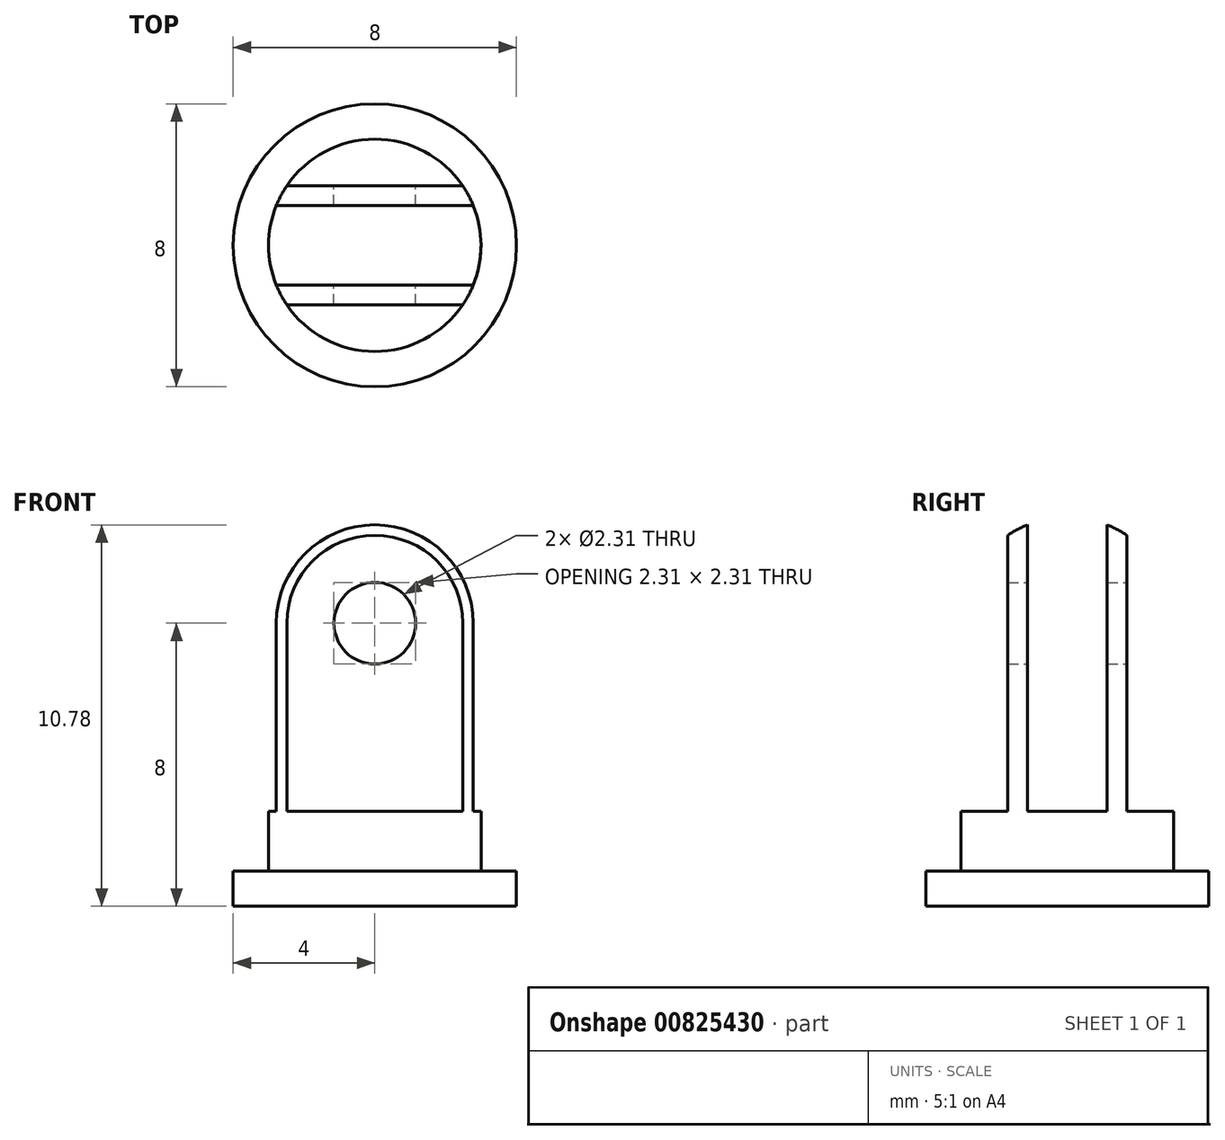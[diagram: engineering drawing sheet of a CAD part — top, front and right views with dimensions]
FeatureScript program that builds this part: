
annotation { "Feature Type Name" : "Feature", "Feature Type Description" : "" }
export const myFeature = defineFeature(function(context is Context, id is Id, definition is map)
    precondition{}
    {
        {
            var Q0;
            Q0=qCreatedBy(makeId("Top.planeOp"),FACE);
            var sketch = newSketch(context, id + "F0", { "sketchPlane" : qUnion([Q0])});
            skCircle(sketch, "E0", {"center": v(0, 0) * mm, "radius": 4 * mm});
            skSolve(sketch);
        }
        {
            var Q0;
            Q0=makeQuery(id+"F0.imprint","IMPRINT",FACE,{"disambiguationData":[TD([[makeQuery(id+"F0.imprint","IMPRINT",EDGE,{"derivedFrom":sQuery(id+"F0.wireOp",EDGE,"E0")}),1.0]])]});
            extrude(context, id + "F1", {"entities" : qUnion([Q0]), "depth" : 1 * mm, "offsetDistance" : 25 * mm});
        }
        {
            var Q0;
            Q0=makeQuery(id+"F1.opExtrude","CAP_FACE",FACE,{"disambiguationData":[OSD([sQuery(id+"F0.wireOp",EDGE,"E0")])],"isStart":false});
            var sketch = newSketch(context, id + "F2", { "sketchPlane" : qUnion([Q0])});
            skCircle(sketch, "E1", {"center": v(0, 0) * mm, "radius": 3 * mm});
            skSolve(sketch);
        }
        {
            var Q0;
            Q0=makeQuery(id+"F2.imprint","IMPRINT",FACE,{"disambiguationData":[TD([[makeQuery(id+"F2.imprint","IMPRINT",EDGE,{"derivedFrom":sQuery(id+"F2.wireOp",EDGE,"E1")}),1.0]])]});
            extrude(context, id + "F3", {"entities" : qUnion([Q0]), "operationType" : NewBodyOperationType.ADD, "depth" : 10 * mm, "offsetDistance" : 25 * mm});
        }
        {
            var Q0;
            Q0=makeQuery(id+"F3.opExtrude","CAP_EDGE",EDGE,{"disambiguationData":[OSD([sQuery(id+"F2.wireOp",EDGE,"E1")])],"isStart":false});
            fillet(context, id + "F4", {"entities" : qUnion([Q0]), "radius" : 3 * mm, "tangentPropagation" : true, "allowEdgeOverflow" : false});
        }
        {
            var Q0;
            Q0=qCreatedBy(makeId("Right.planeOp"),FACE);
            var sketch = newSketch(context, id + "F5", { "sketchPlane" : qUnion([Q0])});
            skLineSegment(sketch, "E2", {"start": v(0, 29.4) * mm, "end": v(0, 0) * mm, "construction": true});
            skLineSegment(sketch, "E3.bottom", {"start": v(1.12, 2.68) * mm, "end": v(-1.12, 2.68) * mm});
            skLineSegment(sketch, "E3.top", {"start": v(1.12, 13.42) * mm, "end": v(-1.12, 13.42) * mm});
            skLineSegment(sketch, "E3.left", {"start": v(1.12, 2.68) * mm, "end": v(1.12, 13.42) * mm});
            skLineSegment(sketch, "E3.right", {"start": v(-1.12, 2.68) * mm, "end": v(-1.12, 13.42) * mm});
            skPoint(sketch, "E3.middle", {"position": v(0, 8.05) * mm});
            skLineSegment(sketch, "E4.bottom", {"start": v(-1.68, 13.42) * mm, "end": v(-3.14, 13.42) * mm});
            skLineSegment(sketch, "E4.top", {"start": v(-1.68, 2.68) * mm, "end": v(-3.14, 2.68) * mm});
            skLineSegment(sketch, "E4.left", {"start": v(-1.68, 13.42) * mm, "end": v(-1.68, 2.68) * mm});
            skLineSegment(sketch, "E4.right", {"start": v(-3.14, 13.42) * mm, "end": v(-3.14, 2.68) * mm});
            skPoint(sketch, "E4.middle", {"position": v(-2.4, 8.05) * mm});
            skPoint(sketch, "E5.middle", {"position": v(2.31, 8.05) * mm});
            skPoint(sketch, "E5.middle.positionSnap0", {"position": v(1.12, 8.05) * mm});
            skPoint(sketch, "E5.centerSnap0", {"position": v(1.12, 8.05) * mm});
            skPoint(sketch, "E5.right.start.orphan", {"position": v(3.1, 13.42) * mm});
            skPoint(sketch, "E5.top.end.orphan", {"position": v(3.1, 2.68) * mm});
            skPoint(sketch, "E5.left.end.orphan", {"position": v(1.53, 2.68) * mm});
            skPoint(sketch, "E5.left.start.orphan", {"position": v(1.53, 13.42) * mm});
            skLineSegment(sketch, "E6.MirrorCS", {"start": v(1.68, 13.42) * mm, "end": v(1.68, 2.68) * mm});
            skLineSegment(sketch, "E7.MirrorCS", {"start": v(1.68, 13.42) * mm, "end": v(3.14, 13.42) * mm});
            skLineSegment(sketch, "E8.MirrorCS", {"start": v(3.14, 13.42) * mm, "end": v(3.14, 2.68) * mm});
            skLineSegment(sketch, "E9.MirrorCS", {"start": v(1.68, 2.68) * mm, "end": v(3.14, 2.68) * mm});
            skSolve(sketch);
        }
        {
            var Q0;
            Q0 = qSketchRegion(id + "F5", true);
            extrude(context, id + "F6", {"entities" : qUnion([Q0]), "operationType" : NewBodyOperationType.REMOVE, "endBound" : BoundingType.SYMMETRIC, "depth" : 25 * mm, "offsetDistance" : 25 * mm});
        }
        {
            var Q0;
            Q0=makeQuery(id+"F6.boolean.opBoolean","COPY",FACE,{"derivedFrom":makeQuery(id+"F6.opExtrude","SWEPT_FACE",FACE,{"disambiguationData":[OSD([sQuery(id+"F5.wireOp",EDGE,"E6.MirrorCS")])]})});
            var sketch = newSketch(context, id + "F7", { "sketchPlane" : qUnion([Q0])});
            skCircle(sketch, "E10", {"center": v(0, 8) * mm, "radius": 1.15 * mm});
            skSolve(sketch);
        }
        {
            var Q0;
            Q0=makeQuery(id+"F7.imprint","IMPRINT",FACE,{"disambiguationData":[TD([[makeQuery(id+"F7.imprint","IMPRINT",EDGE,{"derivedFrom":sQuery(id+"F7.wireOp",EDGE,"E10")}),1.0]])]});
            var Q1;
            Q1=sQuery(id+"F7.wireOp",EDGE,"E10");
            extrude(context, id + "F8", {"entities" : qUnion([Q0]), "operationType" : NewBodyOperationType.REMOVE, "surfaceEntities" : qUnion([Q1]), "oppositeDirection" : true, "depth" : 25 * mm, "offsetDistance" : 25 * mm});
        }
    });
